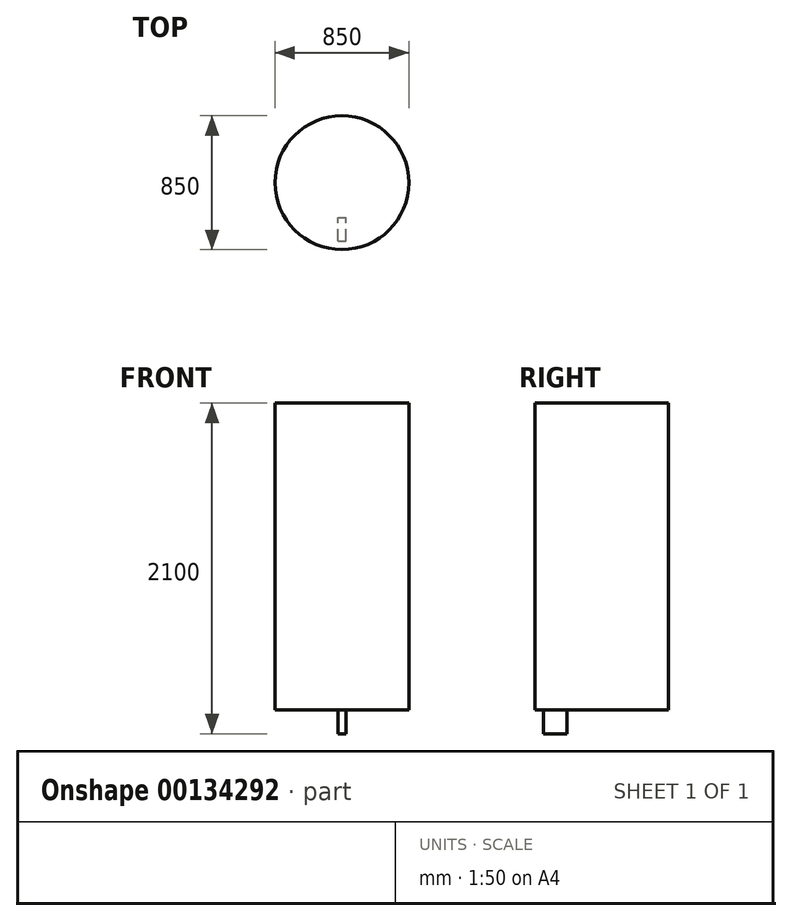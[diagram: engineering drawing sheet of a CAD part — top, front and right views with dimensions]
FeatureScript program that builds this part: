
annotation { "Feature Type Name" : "Feature", "Feature Type Description" : "" }
export const myFeature = defineFeature(function(context is Context, id is Id, definition is map)
    precondition{}
    {
        {
            var Q0;
            Q0=qCreatedBy(makeId("Top.planeOp"),FACE);
            var sketch = newSketch(context, id + "F0", { "sketchPlane" : qUnion([Q0])});
            skCircle(sketch, "E0", {"center": v(0, 0) * mm, "radius": 425 * mm});
            skSolve(sketch);
        }
        {
            var Q0;
            Q0=qSketchRegion(id+"F0",true);
            extrude(context, id + "F1", {"entities" : qUnion([Q0]), "depth" : 1950 * mm});
        }
        {
            var Q0;
            Q0=makeQuery(id+"F1.opExtrude","CAP_FACE",FACE,{"disambiguationData":[OSD([sQuery(id+"F0.wireOp",EDGE,"E0")])],"isStart":true});
            var sketch = newSketch(context, id + "F2", { "sketchPlane" : qUnion([Q0])});
            skLineSegment(sketch, "E1.bottom", {"start": v(-25, 370) * mm, "end": v(25, 370) * mm});
            skLineSegment(sketch, "E1.top", {"start": v(-25, 220) * mm, "end": v(25, 220) * mm});
            skLineSegment(sketch, "E1.left", {"start": v(-25, 370) * mm, "end": v(-25, 220) * mm});
            skLineSegment(sketch, "E1.right", {"start": v(25, 370) * mm, "end": v(25, 220) * mm});
            skSolve(sketch);
        }
        {
            var Q0;
            Q0 = qSketchRegion(id + "F2", true);
            extrude(context, id + "F3", {"entities" : qUnion([Q0]), "operationType" : NewBodyOperationType.ADD, "depth" : 150 * mm});
        }
        {
            var Q0;
            Q0=qCreatedBy(makeId("Front.planeOp"),FACE);
            var sketch = newSketch(context, id + "F4", { "sketchPlane" : qUnion([Q0])});
            skLineSegment(sketch, "E2", {"start": v(0, 0) * mm, "end": v(0, 1982.8) * mm});
            skSolve(sketch);
        }
    });
